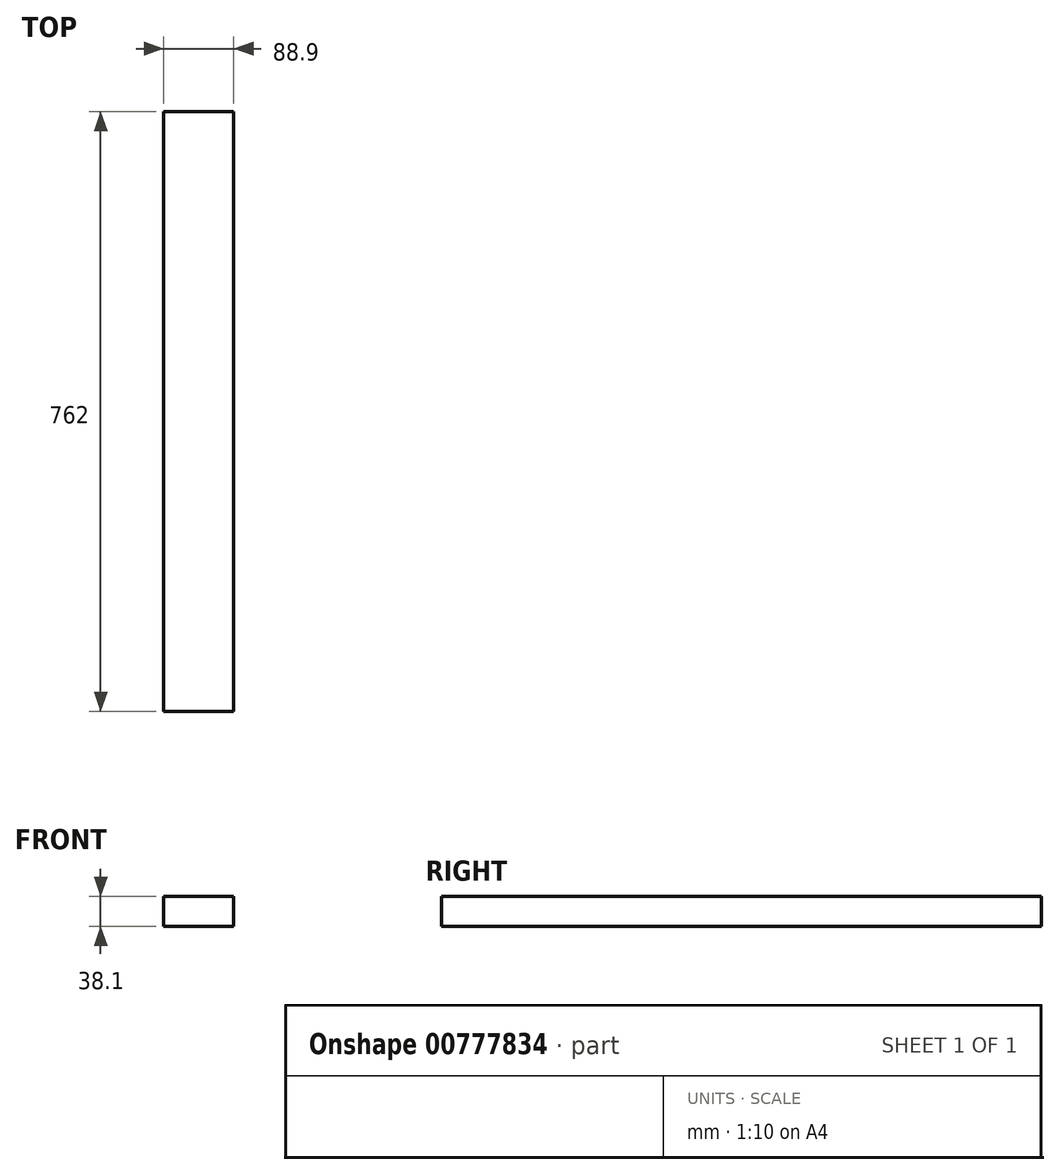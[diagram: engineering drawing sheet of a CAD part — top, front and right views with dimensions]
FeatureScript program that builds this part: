
annotation { "Feature Type Name" : "Feature", "Feature Type Description" : "" }
export const myFeature = defineFeature(function(context is Context, id is Id, definition is map)
    precondition{}
    {
        {
            var Q0;
            Q0=qCreatedBy(makeId("Front.planeOp"),FACE);
            var sketch = newSketch(context, id + "F0", { "sketchPlane" : qUnion([Q0])});
            skLineSegment(sketch, "E0.bottom", {"start": v(44.45, -19.05) * mm, "end": v(-44.45, -19.05) * mm});
            skLineSegment(sketch, "E0.top", {"start": v(44.45, 19.05) * mm, "end": v(-44.45, 19.05) * mm});
            skLineSegment(sketch, "E0.left", {"start": v(44.45, -19.05) * mm, "end": v(44.45, 19.05) * mm});
            skLineSegment(sketch, "E0.right", {"start": v(-44.45, -19.05) * mm, "end": v(-44.45, 19.05) * mm});
            skPoint(sketch, "E0.middle", {"position": v(0, 0) * mm});
            skSolve(sketch);
        }
        {
            var Q0;
            Q0 = qSketchRegion(id + "F0", true);
            extrude(context, id + "F1", {"entities" : qUnion([Q0]), "endBound" : BoundingType.SYMMETRIC, "depth" : 762 * mm, "offsetDistance" : 25.4 * mm});
        }
    });
